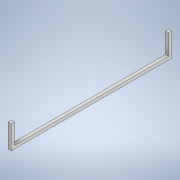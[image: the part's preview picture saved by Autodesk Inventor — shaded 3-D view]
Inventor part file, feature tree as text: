
AUTODESK INVENTOR PART (.ipt)
format: ipt  version: 2020.2 (Build 242310000, 310)  size: 108,544 bytes
history: native  units: mm
features: extrude x2, sketch x1
ambient origin geometry x8: Origin, YZ Plane, XZ Plane, XY Plane, X Axis, Y Axis, Z Axis, Center Point
bodies: Solid1 (feature_tree)
feature tree (3):
  sketch  "Sketch1"  dims[d0=4.0mm d1=197.612mm d2=4.0mm d3=4.0mm d4=4.0mm d5=4.0mm d6=30.0mm d7=0.0mm d8=4.0mm d9=0.0mm]
  extrude  "Extrusion1"  Depth=197.612mm
  extrude  "Extrusion2"  Depth=4.0mm
